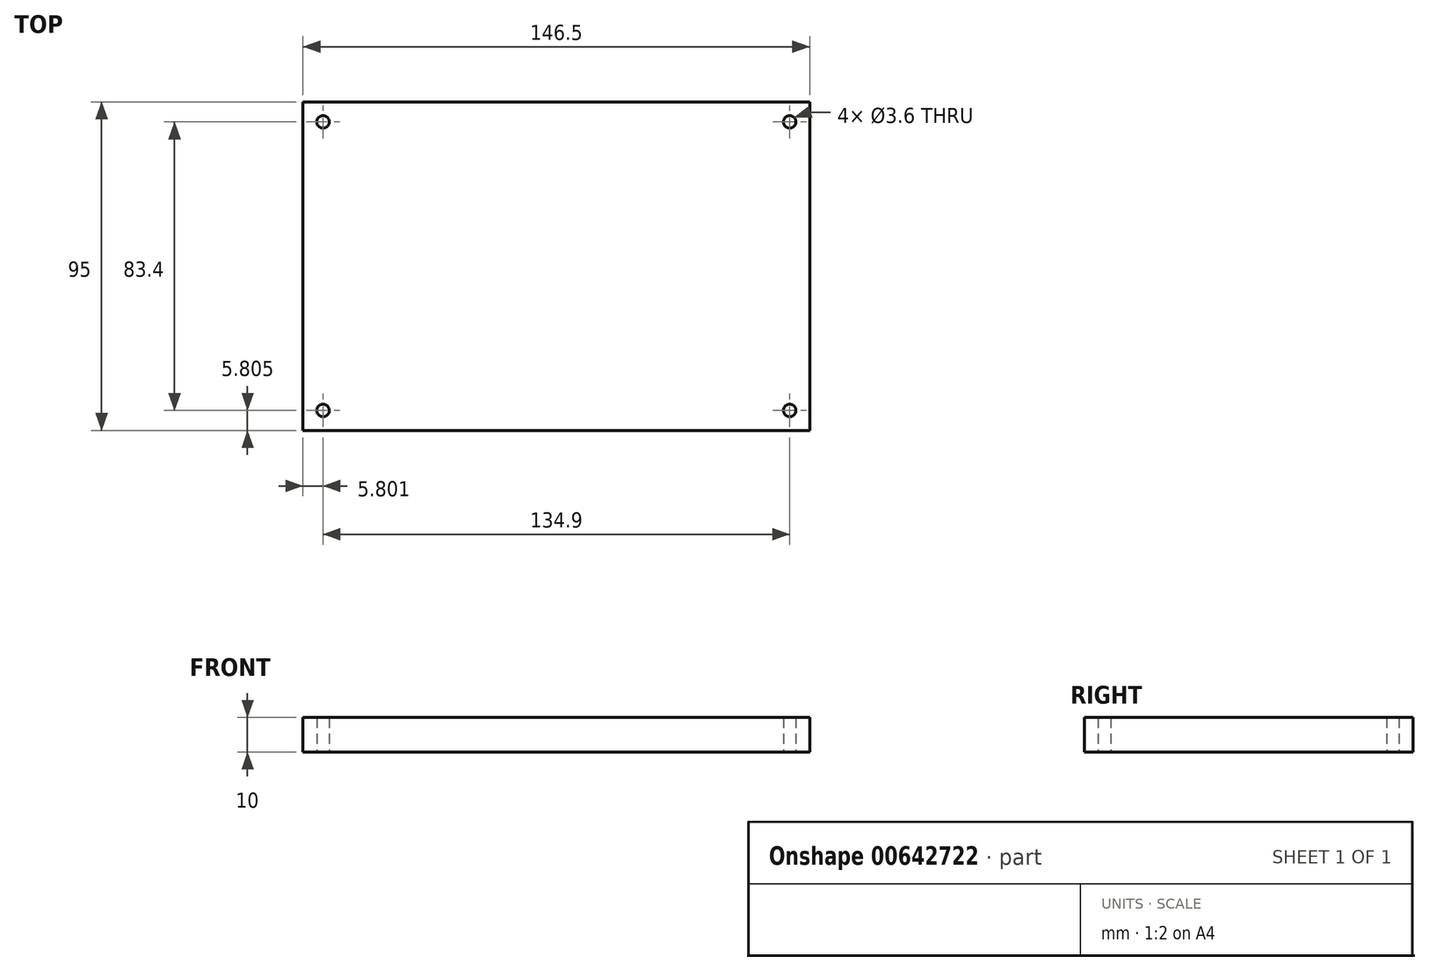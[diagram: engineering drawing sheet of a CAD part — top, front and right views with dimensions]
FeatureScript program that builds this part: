
annotation { "Feature Type Name" : "Feature", "Feature Type Description" : "" }
export const myFeature = defineFeature(function(context is Context, id is Id, definition is map)
    precondition{}
    {
        {
            var Q0;
            Q0=qCreatedBy(makeId("Top.planeOp"),FACE);
            var sketch = newSketch(context, id + "F0", { "sketchPlane" : qUnion([Q0])});
            skLineSegment(sketch, "E0.bottom", {"start": v(-77.57, 38.87) * mm, "end": v(68.93, 38.87) * mm});
            skLineSegment(sketch, "E0.top", {"start": v(-77.57, -56.13) * mm, "end": v(68.93, -56.13) * mm});
            skLineSegment(sketch, "E0.left", {"start": v(-77.57, 38.87) * mm, "end": v(-77.57, -56.13) * mm});
            skLineSegment(sketch, "E0.right", {"start": v(68.93, 38.87) * mm, "end": v(68.93, -56.13) * mm});
            skCircle(sketch, "E1", {"center": v(-71.77, 33.07) * mm, "radius": 1.8 * mm});
            skCircle(sketch, "E2", {"center": v(-71.77, -50.33) * mm, "radius": 1.8 * mm});
            skCircle(sketch, "E3", {"center": v(63.13, -50.33) * mm, "radius": 1.8 * mm});
            skCircle(sketch, "E4", {"center": v(63.13, 33.07) * mm, "radius": 1.8 * mm});
            skSolve(sketch);
        }
        {
            var Q0;
            Q0=makeQuery(id+"F0.imprint","IMPRINT",FACE,{"disambiguationData":[TD([[makeQuery(id+"F0.imprint","IMPRINT",EDGE,{"derivedFrom":sQuery(id+"F0.wireOp",EDGE,"E0.bottom")}),-1.0]])]});
            extrude(context, id + "F1", {"entities" : qUnion([Q0]), "depth" : 10 * mm, "offsetDistance" : 25 * mm});
        }
    });
